# Revit family: Door_Swing_UltiGroup_4500 Series - Double Leaf
name_source: partatom
category: Doors
units: mm (PartAtom-declared; Revit-internal decimal feet)

## family parameters
Always vertical = Yes
Cut with Voids When Loaded = No
Host = Wall
OmniClass Number = 23.30.10.21.31.17
OmniClass Title = Rigid Panel Traffic Doors
Room Calculation Point = No
Shared = No

## types (1)
- Type 1
    Buffer height = 900 mm  [stored 2.95276 ft]
    Define Thermal Properties by = Schematic Type
    Description = 4500 Series Swing Door - Double Leaf
    Door Frame thickness = 3 mm  [stored 0.00984252 ft]
    Door frame width = 60 mm
    DoorFrameFinish_ANZRS = Anodised Aluminium
    DoorFrameMaterial_ANZRS = Door Frame material
    DoorFrameType_ANZRS = Aluminium profile
    DoorGlazingHeight_ANZRS = 0 mm  [stored 0 ft]
    DoorGlazingWidth_ANZRS = 0 mm  [stored 0 ft]
    DoorGrilleHeight_ANZRS = 0 mm  [stored 0 ft]
    DoorGrilleWidth_ANZRS = 0 mm  [stored 0 ft]
    DoorGrille_ANZRS = No
    DoorNumberOfPanels_ANZRS = 0
    DoorOperation_ANZRS = Swing bothways
    DoorPanelBWidth_ANZRS = 0 mm  [stored 0 ft]
    DoorPanelDepth_ANZRS = 0 mm  [stored 0 ft]
    DoorPanelFinish_ANZRS = 45mm Heavy duty polyethylene insulated panel
    DoorPanelHeight_ANZRS = 2400 mm  [stored 7.87402 ft]
    DoorPanelMaterial_ANZRS = Door Panel material
    DoorPanelWidth_ANZRS = 1200 mm
    Fax = 07 846 2467
    Folded Aluminium frame = Door Jamb frame finish
    Function = Interior
    Height = 2400 mm  [stored 7.87402 ft]
    Impact Buffer Colour 1 = Buffer Colour
    Impact Buffer Colour 2 = Buffer Colour
    Impact Buffer width = 1037 mm  [stored 3.40223 ft]
    InstallationGroup_ANZRS = 0
    Manufacturer = Ulti Group Ltd.
    Model = Ulti 4500 Series Swing Door
    ModifiedIssue_ANZRS = 0 $
    Send message = http://ultigroup.co.nz
    Sill Height = 15 mm  [stored 0.0492126 ft]
    URL = www.ultigroup.co.nz
    Vision Panel height = 1000 mm  [stored 3.28084 ft]
    Wall Closure = By host
    Width = 2400 mm  [stored 7.87402 ft]

note: [stored X ft] marks values corroborated as IEEE doubles in the binary element streams (Revit-internal decimal feet)

## geometry (parser evidence)
native form markers: Blend x4, Sweep x14
no freeform markers — native parametric forms only
